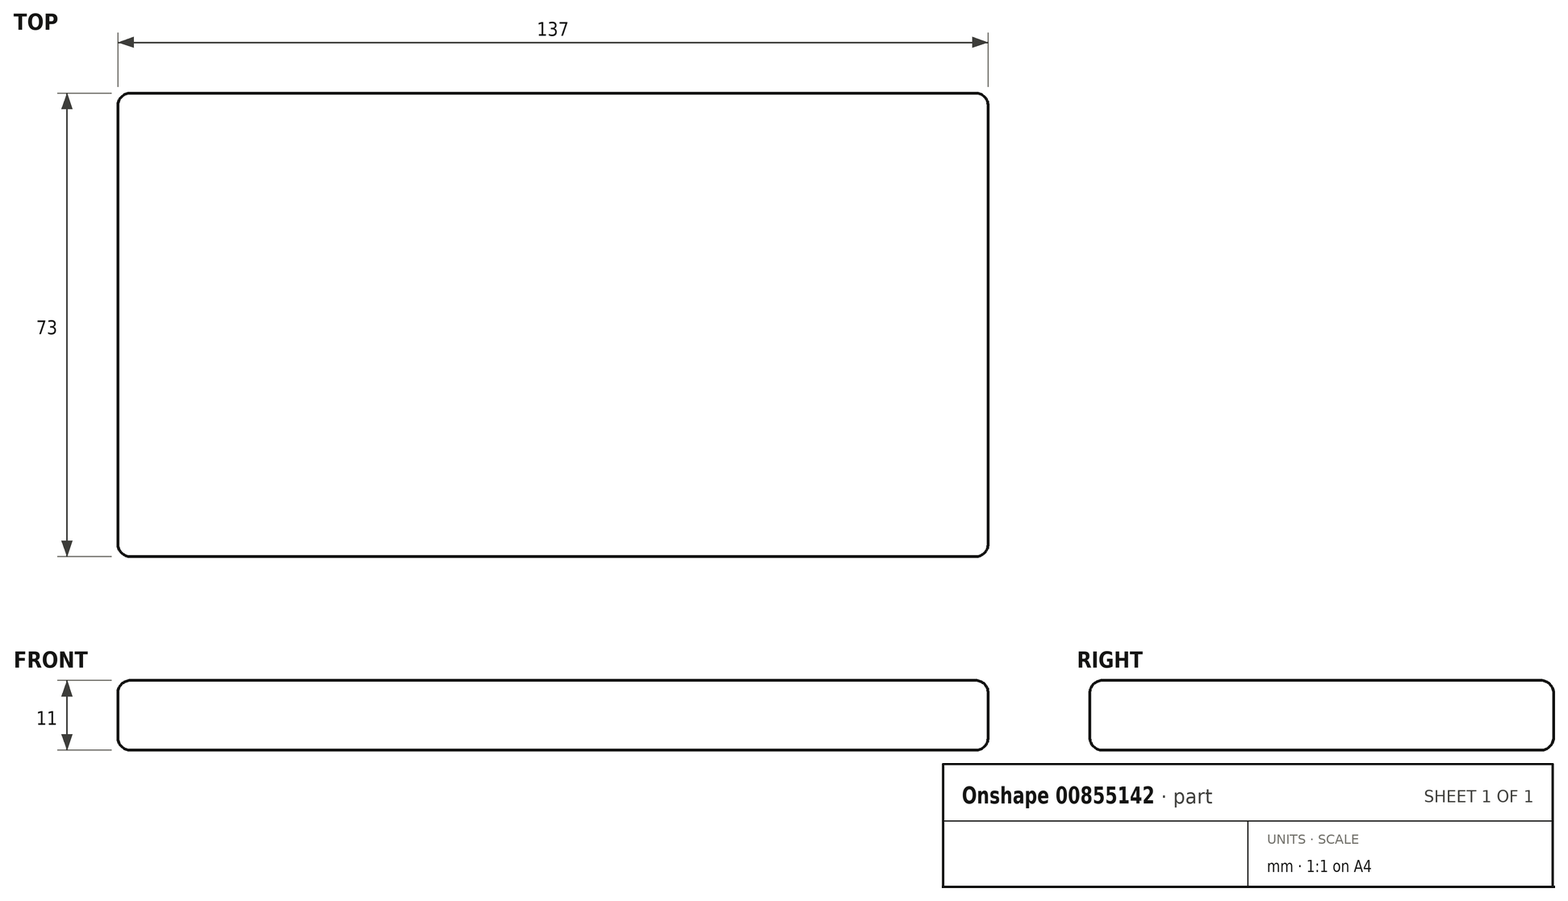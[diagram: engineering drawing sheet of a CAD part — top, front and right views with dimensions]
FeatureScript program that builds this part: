
annotation { "Feature Type Name" : "Feature", "Feature Type Description" : "" }
export const myFeature = defineFeature(function(context is Context, id is Id, definition is map)
    precondition{}
    {
        {
            var Q0;
            Q0=qCreatedBy(makeId("Top.planeOp"),FACE);
            var sketch = newSketch(context, id + "F0", { "sketchPlane" : qUnion([Q0])});
            skLineSegment(sketch, "E0.bottom", {"start": v(-68.5, 36.5) * mm, "end": v(68.5, 36.5) * mm});
            skLineSegment(sketch, "E0.top", {"start": v(-68.5, -36.5) * mm, "end": v(68.5, -36.5) * mm});
            skLineSegment(sketch, "E0.left", {"start": v(-68.5, 36.5) * mm, "end": v(-68.5, -36.5) * mm});
            skLineSegment(sketch, "E0.right", {"start": v(68.5, 36.5) * mm, "end": v(68.5, -36.5) * mm});
            skSolve(sketch);
        }
        {
            var Q0;
            Q0=qSketchRegion(id+"F0",true);
            extrude(context, id + "F1", {"entities" : qUnion([Q0]), "depth" : 11 * mm, "offsetDistance" : 25 * mm});
        }
        {
            var Q0;
            Q0=makeQuery(id+"F1.opExtrude","CAP_EDGE",EDGE,{"disambiguationData":[OSD([sQuery(id+"F0.wireOp",EDGE,"E0.left")])],"isStart":false});
            var Q1;
            Q1=makeQuery(id+"F1.opExtrude","SWEPT_EDGE",EDGE,{"disambiguationData":[OSD([sQuery(id+"F0.wireOp",EDGE,"E0.top"),sQuery(id+"F0.wireOp",EDGE,"E0.left")])]});
            var Q2;
            Q2=makeQuery(id+"F1.opExtrude","CAP_EDGE",EDGE,{"disambiguationData":[OSD([sQuery(id+"F0.wireOp",EDGE,"E0.top")])],"isStart":false});
            var Q3;
            Q3=makeQuery(id+"F1.opExtrude","CAP_EDGE",EDGE,{"disambiguationData":[OSD([sQuery(id+"F0.wireOp",EDGE,"E0.bottom")])],"isStart":false});
            var Q4;
            Q4=makeQuery(id+"F1.opExtrude","CAP_EDGE",EDGE,{"disambiguationData":[OSD([sQuery(id+"F0.wireOp",EDGE,"E0.bottom")])],"isStart":true});
            var Q5;
            Q5=makeQuery(id+"F1.opExtrude","SWEPT_EDGE",EDGE,{"disambiguationData":[OSD([sQuery(id+"F0.wireOp",EDGE,"E0.bottom"),sQuery(id+"F0.wireOp",EDGE,"E0.left")])]});
            var Q6;
            Q6=makeQuery(id+"F1.opExtrude","CAP_EDGE",EDGE,{"disambiguationData":[OSD([sQuery(id+"F0.wireOp",EDGE,"E0.left")])],"isStart":true});
            var Q7;
            Q7=makeQuery(id+"F1.opExtrude","CAP_EDGE",EDGE,{"disambiguationData":[OSD([sQuery(id+"F0.wireOp",EDGE,"E0.top")])],"isStart":true});
            var Q8;
            Q8=makeQuery(id+"F1.opExtrude","CAP_EDGE",EDGE,{"disambiguationData":[OSD([sQuery(id+"F0.wireOp",EDGE,"E0.right")])],"isStart":true});
            var Q9;
            Q9=makeQuery(id+"F1.opExtrude","SWEPT_EDGE",EDGE,{"disambiguationData":[OSD([sQuery(id+"F0.wireOp",EDGE,"E0.top"),sQuery(id+"F0.wireOp",EDGE,"E0.right")])]});
            var Q10;
            Q10=makeQuery(id+"F1.opExtrude","SWEPT_EDGE",EDGE,{"disambiguationData":[OSD([sQuery(id+"F0.wireOp",EDGE,"E0.bottom"),sQuery(id+"F0.wireOp",EDGE,"E0.right")])]});
            var Q11;
            Q11=makeQuery(id+"F1.opExtrude","CAP_EDGE",EDGE,{"disambiguationData":[OSD([sQuery(id+"F0.wireOp",EDGE,"E0.right")])],"isStart":false});
            fillet(context, id + "F2", {"entities" : qUnion([Q0, Q1, Q2, Q3, Q4, Q5, Q6, Q7, Q8, Q9, Q10, Q11]), "radius" : 2 * mm, "tangentPropagation" : true, "allowEdgeOverflow" : false});
        }
    });
